# Revit family: Bitpop 4.1A
name_source: partatom
category: Lighting Fixtures
revit_build: Autodesk Revit 2017 (Build: 20160225_1515(x64)
units: mm (PartAtom-declared; Revit-internal decimal feet)

## family parameters
Cut with Voids When Loaded = Yes
Host = Face
Light Source = Yes
Part Type = Normal
Room Calculation Point = Yes
Round Connector Dimension = Use Diameter
Shared = No

## types (8) — shared parameters
Apparent Load Phase 1 = 26 W
Body = L&L_Black anodized aluminium
CRI = 90 (also available: CRI 80 - ref. URL Technical sheet)
Code = BP4110 B White; BP4110 N Black; BP4111 B White; BP4111 N Black
Color Filter = 16777215
Control system = on/off; 1-10V + PUSH; DALI + PUSH
Cutout dimensions = 162x42 mm
Default Elevation = 1219 mm
Delivered lumen output = 992 lm (3000K, 30°, 18W); 1340 lm (3000K, 30°, 26W)
Description = Indoor recessed
Dimming Lamp Color Temperature Shift = <None>
Emit from Line Length = 610 mm
Energy efficiency class = A A+ A++
Features = UGR < 10 for 17° and 30° optics
Height mm = 71 mm  [stored 0.23294 ft]
Height void = 42 mm  [stored 0.137795 ft]
IP = 40; 44 installed
Length mm = 169 mm  [stored 0.554462 ft]
Lens = L&L_Lens
Lumen output at source = 1400 lm (3000K, 18W); 1920 lm (3000K, 26W)
Manufacturer = L&L Luce&Light
Material = body in black anodized aluminium trim in steel
Mounting = recessed (ceiling: flush or deep set)
No. and type of led = 4 high-intensity power LEDs
Notes = ceiling-mounted version Bitpop C
Power = 26W (also available: 18W - ref. URL Technical sheet)
Power cables = includes 0.30 m cable
Power supply = 230Vac
Power supply unit = included and wired
Tilt Angle = 90.00°
Trim = L&L_Steel
URL = https://www.lucelight.it
URL Accessories and power supply units = https://www.lucelight.it
URL Catalogue = https://www.lucelight.it
URL DXF = https://www.lucelight.it
URL Description = https://www.lucelight.it
URL General code = https://www.lucelight.it
URL IES Photometric file = https://www.lucelight.it
URL Image = https://www.lucelight.it
URL Technical sheet = https://www.lucelight.it
Voltage = 230 V
Weight kg = 0.42
Width mm = 49 mm  [stored 0.160761 ft]
Wiring = -

## per-type parameters (varying)
| type | Geometry | LED Colour | Length void | Model | Optics | Photometric Web File | Width void |
| Bitpop 4.1_ F 30° (3000K 26W 230Vac) | Bitpop4.1_mod : Bitpop 4.1 | 3000K (also available: 2700K and 4000K - ref. URL Technical sheet) | 162 mm  [stored 0.531496 ft] | Bitpop 4.1 | 30° | BITPOP 4.1 F 30° [3000K 26W 230Vac].IES | 42 mm  [stored 0.137795 ft] |
| Bitpop 4.1_ L 42° (3000K 26W 230Vac) | Bitpop4.1_mod : Bitpop 4.1 | 3000K (also available: 2700K and 4000K - ref. URL Technical sheet) | 162 mm  [stored 0.531496 ft] | Bitpop 4.1 | 42° | BITPOP 4.1 L 42° [3000K 26W 230Vac].IES | 42 mm  [stored 0.137795 ft] |
| Bitpop 4.1_ S 17° (3000K 26W 230Vac) | Bitpop4.1_mod : Bitpop 4.1 | 3000K (also available: 2700K and 4000K - ref. URL Technical sheet) | 162 mm  [stored 0.531496 ft] | Bitpop 4.1 | 17° | BITPOP 4.1 S 17° [3000K 26W 230Vac].IES | 42 mm  [stored 0.137795 ft] |
| Bitpop 4.1_ W 17°x45° (3000K 26W 230Vac) | Bitpop4.1_mod : Bitpop 4.1 | 3000K (also available: 2700K and 4000K - ref. URL Technical sheet) | 162 mm  [stored 0.531496 ft] | Bitpop 4.1 | 17°x45° | BITPOP 4.1 W 17°x45° [3000K 26W 230Vac].IES | 42 mm  [stored 0.137795 ft] |
| Bitpop 4.1_Recessed_ F 30° (3000K 26W 230Vac) | Bitpop4.1_Recessed_mod : Bitpop 4.1 recessed | 3000K (also available: 2700K and 4000K - ref. URL Technical sheet) | 173 mm  [stored 0.567585 ft] | Bitpop 4.1_Recessed | 30° | BITPOP 4.1 F 30° [3000K 26W 230Vac].IES | 53 mm  [stored 0.173885 ft] |
| Bitpop 4.1_Recessed_ L 42° (3000K 26W 230Vac) | Bitpop4.1_Recessed_mod : Bitpop 4.1 recessed | 3000K (also available: 2700K and 4000K - ref. URL Technical sheet) | 173 mm  [stored 0.567585 ft] | Bitpop 4.1_Recessed | 42° | BITPOP 4.1 L 42° [3000K 26W 230Vac].IES | 53 mm  [stored 0.173885 ft] |
| Bitpop 4.1_Recessed_ S 17° (3000K 26W 230Vac) | Bitpop4.1_Recessed_mod : Bitpop 4.1 recessed | 3000K (also available: 2700K and 4000K - ref. URL Technical sheet) | 173 mm  [stored 0.567585 ft] | Bitpop 4.1_Recessed | 17° | BITPOP 4.1 S 17° [3000K 26W 230Vac].IES | 53 mm  [stored 0.173885 ft] |
| Bitpop 4.1_Recessed_ W 17°x45° (3000K 26W 230Vac) | Bitpop4.1_Recessed_mod : Bitpop 4.1 recessed | 3000K (also available: 2700K and 4000K - ref. URL Technical sheet) | 173 mm  [stored 0.567585 ft] | Bitpop 4.1_Recessed | 17°x45° | BITPOP 4.1 W 17°x45° [3000K 26W 230Vac].IES | 53 mm  [stored 0.173885 ft] |

note: [stored X ft] marks values corroborated as IEEE doubles in the binary element streams (Revit-internal decimal feet)

## geometry (parser evidence)
native form markers: Blend x2, Sweep x6
no freeform markers — native parametric forms only
